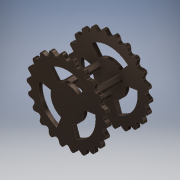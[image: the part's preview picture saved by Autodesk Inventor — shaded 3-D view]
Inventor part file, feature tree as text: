
AUTODESK INVENTOR PART (.ipt)
format: ipt  version: 2019 (Build 230136000, 136)  size: 479,232 bytes
history: native  units: mm
features: extrude x5, sketch x5, pattern_circular x2, projected_geometry x1
ambient origin geometry x8: Origin, YZ Plane, XZ Plane, XY Plane, X Axis, Y Axis, Z Axis, Center Point
bodies: Solid1 (feature_tree)
feature tree (13):
  extrude  "Extrusion1"  Depth=2.5mm TaperAngle=0.0deg
  extrude  "Extrusion2"  Depth=2.5mm TaperAngle=0.0deg
  pattern_circular  "Circular Pattern1"  Count=22 Angle=360.0deg
  extrude  "Extrusion3"  Depth=2.5mm TaperAngle=360.0deg
  pattern_circular  "Circular Pattern2"  [2 undecoded]
  extrude  "Extrusion4"  Depth=2.5mm
  extrude  "Extrusion5"  Depth=2.5mm TaperAngle=360.0deg
  sketch  "Sketch1"  dims[d0=55.0mm d1=2.5mm d2=0.0mm]
  sketch  "Sketch2"  dims[d3=49.0mm d4=2.5mm d5=0.0mm d6=220.0mm d7=360.0deg]
  sketch  "Sketch3"  dims[d10=2.5mm d11=0.0mm d12=30.0mm d13=360.0deg]
  sketch  "Sketch4"  dims[d15=3.0mm]
  sketch  "Sketch5"  dims[d16=3.490659mm d17=8.5mm d18=4.0mm d19=30.0mm d21=360.0deg d23=28.5mm d24=0.0mm d25=2.5mm d26=0.0mm]
  projected_geometry  "Projected Loop1"
note: 2 required parameter values undecoded (feature->parameter linkage not recoverable at this tier; creation-order binding heuristic only, values carry confidence <= 0.55)
